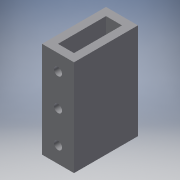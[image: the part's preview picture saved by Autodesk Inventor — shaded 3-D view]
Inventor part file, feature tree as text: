
AUTODESK INVENTOR PART (.ipt)
format: ipt  version: 2017 (Build 210142000, 142)  size: 123,392 bytes
history: native  units: in
note: dims shown in document units (in); Inventor stores cm internally (conversion verified against a paired STEP export)
features: extrude x3, sketch x3, projected_geometry x1
ambient origin geometry x8: Origin, YZ Plane, XZ Plane, XY Plane, X Axis, Y Axis, Z Axis, Center Point
bodies: Solid1 (feature_tree)
feature tree (7):
  extrude  "Extrusion1"  Depth=1.0in
  extrude  "Extrusion2"  Depth=0.25in
  extrude  "Extrusion3"  Depth=0.25in
  sketch  "Sketch1"  dims[d0=3.0in d1=1.0in]
  sketch  "Sketch2"  dims[d2=2.0in d3=0.0in d4=0.25in]
  projected_geometry  "Projected Loop1"
  sketch  "Sketch3"  dims[d5=2.0in d6=0.0in d7=0.25in d8=0.5in d9=1.1811in d11=1.0in d12=0.3937in d14=1.0in d16=2.0in d17=0.0in]
